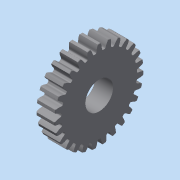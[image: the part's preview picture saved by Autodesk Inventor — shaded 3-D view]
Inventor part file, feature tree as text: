
AUTODESK INVENTOR PART (.ipt)
format: ipt  version: 2015 (Build 190159000, 159)  size: 1,117,696 bytes
history: native  units: in
note: dims shown in document units (in); Inventor stores cm internally (conversion verified against a paired STEP export)
features: other x1, plane x1, split x1, imported_body x1
ambient origin geometry x8: Origin, YZ Plane, XZ Plane, XY Plane, X Axis, Y Axis, Z Axis, Center Point
bodies: Solid1 (feature_tree)
feature tree (4):
  other  "a_1c_2-n2402731"
  plane  "Work Plane1"
  split  "Split1"
  imported_body  "Base1"
